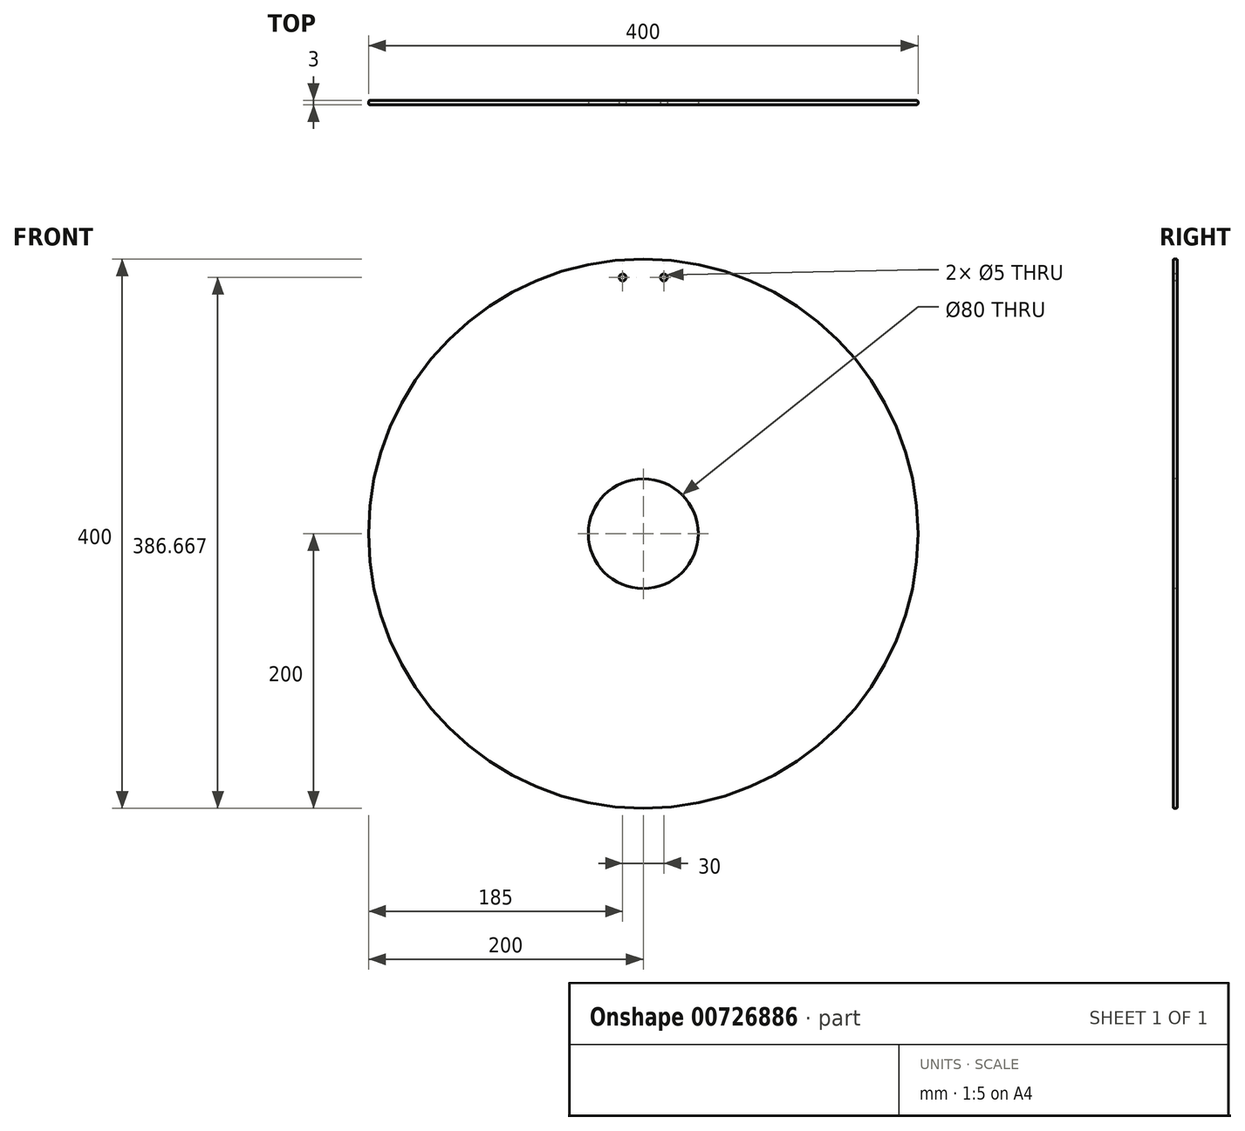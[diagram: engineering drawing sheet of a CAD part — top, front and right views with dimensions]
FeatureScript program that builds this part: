
annotation { "Feature Type Name" : "Feature", "Feature Type Description" : "" }
export const myFeature = defineFeature(function(context is Context, id is Id, definition is map)
    precondition{}
    {
        {
            var Q0;
            Q0=qCreatedBy(makeId("Front.planeOp"),FACE);
            var sketch = newSketch(context, id + "F0", { "sketchPlane" : qUnion([Q0])});
            skCircle(sketch, "E0", {"center": v(0, 0) * mm, "radius": 200 * mm});
            skLineSegment(sketch, "E1", {"start": v(0, 186.67) * mm, "end": v(0, 229.38) * mm, "construction": true});
            skLineSegment(sketch, "E2", {"start": v(0, 229.38) * mm, "end": v(0, 217.26) * mm});
            skLineSegment(sketch, "E3", {"start": v(0, 0) * mm, "end": v(262.39, 0) * mm, "construction": true});
            skLineSegment(sketch, "E4", {"start": v(262.39, 0) * mm, "end": v(-295.93, 0) * mm, "construction": true});
            skLineSegment(sketch, "E5", {"start": v(-295.93, 0) * mm, "end": v(0, 0) * mm, "construction": true});
            skLineSegment(sketch, "E6", {"start": v(0, -235.42) * mm, "end": v(0, 0) * mm, "construction": true});
            skPoint(sketch, "E7", {"position": v(-15, 186.67) * mm});
            skPoint(sketch, "E8", {"position": v(15, 186.67) * mm});
            skLineSegment(sketch, "E9", {"start": v(0, 0) * mm, "end": v(0, 217.26) * mm, "construction": true});
            skLineSegment(sketch, "E10", {"start": v(0, 186.67) * mm, "end": v(15, 186.67) * mm});
            skLineSegment(sketch, "E11", {"start": v(0, 186.67) * mm, "end": v(-15, 186.67) * mm});
            skSolve(sketch);
        }
        {
            var Q0;
            Q0=makeQuery(id+"F0.imprint","IMPRINT",FACE,{"disambiguationData":[TD([[makeQuery(id+"F0.imprint","IMPRINT",EDGE,{"derivedFrom":sQuery(id+"F0.wireOp",EDGE,"E0")}),1.0]])]});
            extrude(context, id + "F1", {"entities" : qUnion([Q0]), "depth" : 3 * mm, "offsetDistance" : 25 * mm});
        }
        {
            var Q0;
            Q0=sQuery(id+"F0.wireOp",VERTEX,"E7");
            var Q1;
            Q1=sQuery(id+"F0.wireOp",VERTEX,"E8");
            var Q2;
            Q2=makeQuery(id+"F1.opExtrude","SWEPT_BODY",BODY,{"disambiguationData":[OSD([sQuery(id+"F0.wireOp",EDGE,"E0")])]});
            hole(context, id + "F2", {"style" : HoleStyle.SIMPLE, "endStyle" : HoleEndStyle.BLIND, "oppositeDirection" : true, "holeDiameter" : 5 * mm, "majorDiameter" : 5 * mm, "holeDepth" : 60 * mm, "isTappedThrough" : true, "tappedDepth" : 12 * mm, "tapClearance" : 3, "startFromSketch" : true, "locations" : qUnion([Q0, Q1]), "scope" : qUnion([Q2])});
        }
        {
            var Q0;
            Q0=makeQuery(id+"F1.opExtrude","CAP_EDGE",EDGE,{"disambiguationData":[OSD([sQuery(id+"F0.wireOp",EDGE,"E0")])],"isStart":false});
            var Q1;
            Q1=makeQuery(id+"F1.opExtrude","CAP_EDGE",EDGE,{"disambiguationData":[OSD([sQuery(id+"F0.wireOp",EDGE,"E0")])],"isStart":true});
            fillet(context, id + "F3", {"entities" : qUnion([Q0, Q1]), "radius" : 1 * mm, "tangentPropagation" : true, "allowEdgeOverflow" : false});
        }
        {
            var Q0;
            Q0=sQuery(id+"F0.wireOp",VERTEX,"E3.start");
            var Q1;
            Q1=makeQuery(id+"F1.opExtrude","SWEPT_BODY",BODY,{"disambiguationData":[OSD([sQuery(id+"F0.wireOp",EDGE,"E0")])]});
            hole(context, id + "F4", {"style" : HoleStyle.SIMPLE, "endStyle" : HoleEndStyle.BLIND, "oppositeDirection" : true, "holeDiameter" : 80 * mm, "majorDiameter" : 5 * mm, "holeDepth" : 60 * mm, "isTappedThrough" : true, "tappedDepth" : 12 * mm, "tapClearance" : 3, "startFromSketch" : true, "locations" : qUnion([Q0]), "scope" : qUnion([Q1])});
        }
    });
